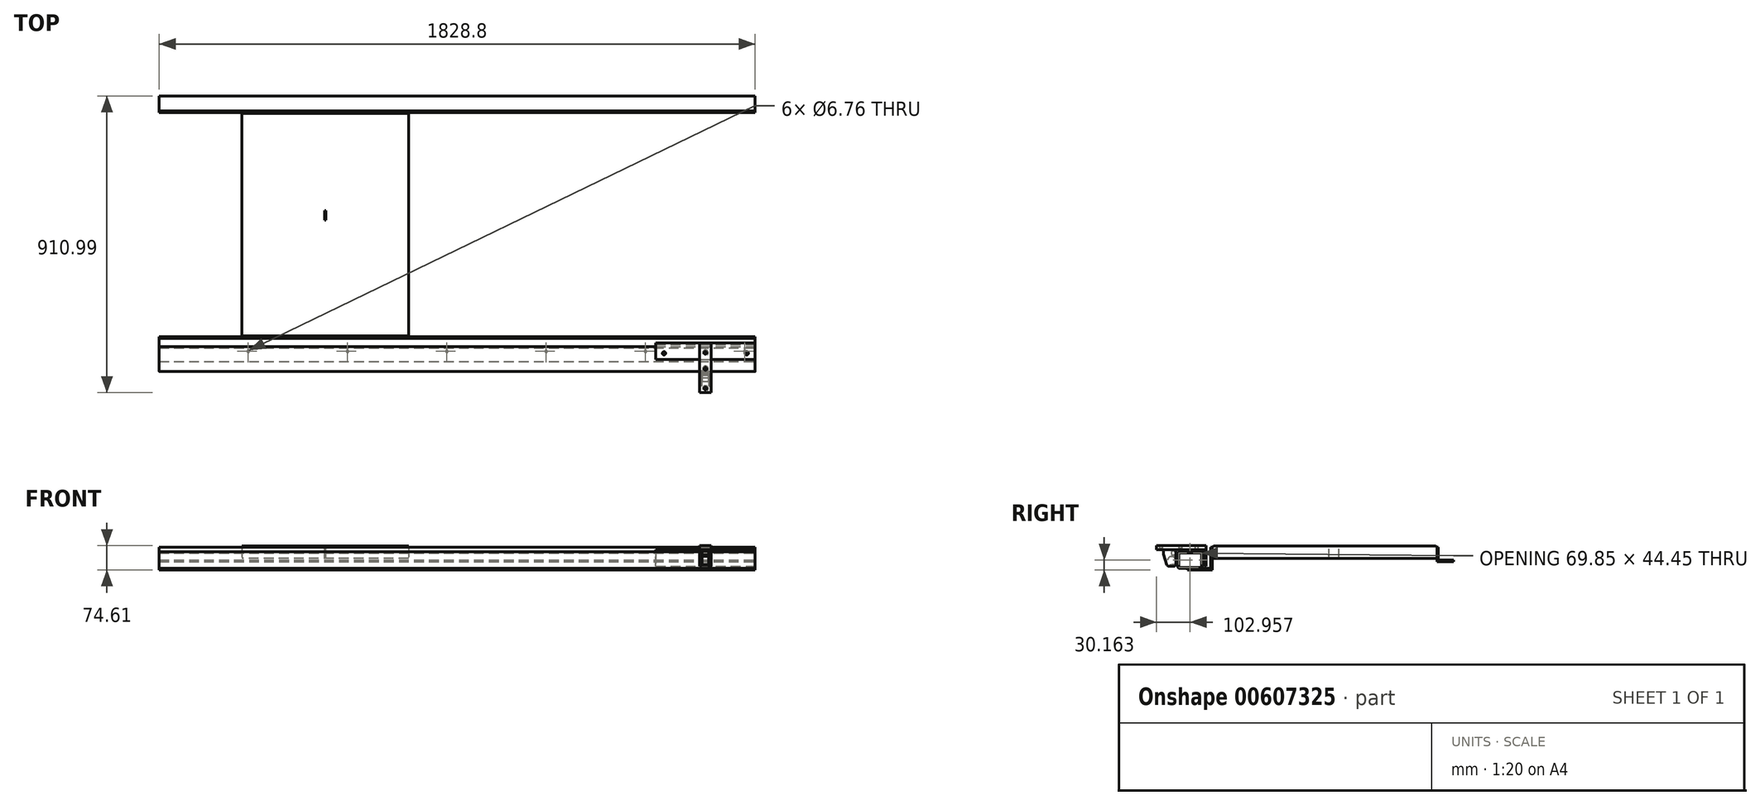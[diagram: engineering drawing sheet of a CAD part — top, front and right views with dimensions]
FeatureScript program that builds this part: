
annotation { "Feature Type Name" : "Feature", "Feature Type Description" : "" }
export const myFeature = defineFeature(function(context is Context, id is Id, definition is map)
    precondition{}
    {
        {
            var Q0;
            Q0=qCreatedBy(makeId("Right.planeOp"),FACE);
            var sketch = newSketch(context, id + "F0", { "sketchPlane" : qUnion([Q0])});
            skLineSegment(sketch, "E0", {"start": v(-76.2, 0) * mm, "end": v(0, 0) * mm});
            skLineSegment(sketch, "E1", {"start": v(0, 0) * mm, "end": v(0, 69.85) * mm});
            skLineSegment(sketch, "E2", {"start": v(0, 69.85) * mm, "end": v(-4.76, 69.85) * mm});
            skLineSegment(sketch, "E3", {"start": v(-4.76, 69.85) * mm, "end": v(-4.76, 4.76) * mm});
            skLineSegment(sketch, "E4", {"start": v(-4.76, 4.76) * mm, "end": v(-76.2, 4.76) * mm});
            skLineSegment(sketch, "E5", {"start": v(-76.2, 4.76) * mm, "end": v(-76.2, 0) * mm});
            skSolve(sketch);
        }
        {
            var Q0;
            Q0 = qSketchRegion(id + "F0", true);
            extrude(context, id + "F1", {"entities" : qUnion([Q0]), "oppositeDirection" : true, "depth" : 1828.8 * mm, "offsetDistance" : 25.4 * mm});
        }
        {
            var Q0;
            Q0=qCreatedBy(makeId("Right.planeOp"),FACE);
            var sketch = newSketch(context, id + "F2", { "sketchPlane" : qUnion([Q0])});
            skLineSegment(sketch, "E6.0", {"start": v(-4.76, 4.76) * mm, "end": v(-76.2, 4.76) * mm});
            skLineSegment(sketch, "E7.bottom", {"start": v(-36.51, 4.76) * mm, "end": v(-100.01, 4.76) * mm});
            skLineSegment(sketch, "E7.top", {"start": v(-36.51, 55.56) * mm, "end": v(-100.01, 55.56) * mm});
            skLineSegment(sketch, "E7.left", {"start": v(-30.16, 11.11) * mm, "end": v(-30.16, 49.21) * mm});
            skLineSegment(sketch, "E7.right", {"start": v(-106.36, 11.11) * mm, "end": v(-106.36, 49.21) * mm});
            skLineSegment(sketch, "E8.bottom", {"start": v(-100.01, 52.39) * mm, "end": v(-36.51, 52.39) * mm});
            skLineSegment(sketch, "E8.top", {"start": v(-100.01, 7.94) * mm, "end": v(-36.51, 7.94) * mm});
            skLineSegment(sketch, "E8.left", {"start": v(-103.19, 49.21) * mm, "end": v(-103.19, 11.11) * mm});
            skLineSegment(sketch, "E8.right", {"start": v(-33.34, 49.21) * mm, "end": v(-33.34, 11.11) * mm});
            skPoint(sketch, "E9.visualSharp", {"position": v(-106.36, 55.56) * mm});
            skArc(sketch, "E9.filletArc", {"start": v(-100.01, 55.56) * mm, "mid": v(-104.5, 53.7) * mm, "end": v(-106.36, 49.21) * mm});
            skPoint(sketch, "E10.visualSharp", {"position": v(-106.36, 4.76) * mm});
            skArc(sketch, "E10.filletArc", {"start": v(-106.36, 11.11) * mm, "mid": v(-104.5, 6.62) * mm, "end": v(-100.01, 4.76) * mm});
            skPoint(sketch, "E11.visualSharp", {"position": v(-30.16, 4.76) * mm});
            skArc(sketch, "E11.filletArc", {"start": v(-36.51, 4.76) * mm, "mid": v(-32.02, 6.62) * mm, "end": v(-30.16, 11.11) * mm});
            skPoint(sketch, "E12.visualSharp", {"position": v(-30.16, 55.56) * mm});
            skArc(sketch, "E12.filletArc", {"start": v(-30.16, 49.21) * mm, "mid": v(-32.02, 53.7) * mm, "end": v(-36.51, 55.56) * mm});
            skPoint(sketch, "E13.visualSharp", {"position": v(-33.34, 52.39) * mm});
            skArc(sketch, "E13.filletArc", {"start": v(-33.34, 49.21) * mm, "mid": v(-34.27, 51.46) * mm, "end": v(-36.51, 52.39) * mm});
            skPoint(sketch, "E14.visualSharp", {"position": v(-103.19, 52.39) * mm});
            skArc(sketch, "E14.filletArc", {"start": v(-100.01, 52.39) * mm, "mid": v(-102.26, 51.46) * mm, "end": v(-103.19, 49.21) * mm});
            skPoint(sketch, "E15.visualSharp", {"position": v(-103.19, 7.94) * mm});
            skArc(sketch, "E15.filletArc", {"start": v(-103.19, 11.11) * mm, "mid": v(-102.26, 8.87) * mm, "end": v(-100.01, 7.94) * mm});
            skPoint(sketch, "E16.visualSharp", {"position": v(-33.34, 7.94) * mm});
            skArc(sketch, "E16.filletArc", {"start": v(-36.51, 7.94) * mm, "mid": v(-34.27, 8.87) * mm, "end": v(-33.34, 11.11) * mm});
            skSolve(sketch);
        }
        {
            var Q0;
            Q0 = qSketchRegion(id + "F2", true);
            extrude(context, id + "F3", {"entities" : qUnion([Q0]), "oppositeDirection" : true, "depth" : 1828.8 * mm, "offsetDistance" : 25.4 * mm});
        }
        {
            var Q0;
            Q0=qCreatedBy(makeId("Right.planeOp"),FACE);
            var sketch = newSketch(context, id + "F4", { "sketchPlane" : qUnion([Q0])});
            skLineSegment(sketch, "E17.0", {"start": v(-36.51, 55.56) * mm, "end": v(-100.01, 55.56) * mm});
            skLineSegment(sketch, "E18.0", {"start": v(-30.16, 11.11) * mm, "end": v(-30.16, 49.21) * mm});
            skLineSegment(sketch, "E19", {"start": v(-69.62, 57.15) * mm, "end": v(-29.93, 57.15) * mm});
            skLineSegment(sketch, "E20", {"start": v(-23.58, 50.8) * mm, "end": v(-23.58, 11.11) * mm});
            skLineSegment(sketch, "E21", {"start": v(-23.58, 11.11) * mm, "end": v(-18.82, 11.11) * mm});
            skLineSegment(sketch, "E22", {"start": v(-18.82, 11.11) * mm, "end": v(-18.82, 61.91) * mm});
            skLineSegment(sketch, "E23", {"start": v(-18.82, 61.91) * mm, "end": v(-69.62, 61.91) * mm});
            skLineSegment(sketch, "E24", {"start": v(-69.62, 61.91) * mm, "end": v(-69.62, 57.15) * mm});
            skPoint(sketch, "E25.visualSharp", {"position": v(-23.58, 57.15) * mm});
            skArc(sketch, "E25.filletArc", {"start": v(-23.58, 50.8) * mm, "mid": v(-25.44, 55.3) * mm, "end": v(-29.93, 57.15) * mm});
            skSolve(sketch);
        }
        {
            var Q0;
            Q0 = qSketchRegion(id + "F4", true);
            extrude(context, id + "F5", {"entities" : qUnion([Q0]), "oppositeDirection" : true, "depth" : 304.8 * mm, "offsetDistance" : 25.4 * mm});
        }
        {
            var Q0;
            Q0=makeQuery(id+"F5.opExtrude","SWEPT_FACE",FACE,{"disambiguationData":[OSD([sQuery(id+"F4.wireOp",EDGE,"E23")])]});
            var sketch = newSketch(context, id + "F6", { "sketchPlane" : qUnion([Q0])});
            skLineSegment(sketch, "E26", {"start": v(-152.4, -18.82) * mm, "end": v(-152.4, -69.62) * mm, "construction": true});
            skLineSegment(sketch, "E27.bottom", {"start": v(-169.86, -18.82) * mm, "end": v(-134.94, -18.82) * mm});
            skLineSegment(sketch, "E27.top", {"start": v(-169.86, -171.22) * mm, "end": v(-134.94, -171.22) * mm});
            skLineSegment(sketch, "E27.left", {"start": v(-169.86, -18.82) * mm, "end": v(-169.86, -171.22) * mm});
            skLineSegment(sketch, "E27.right", {"start": v(-134.94, -18.82) * mm, "end": v(-134.94, -171.22) * mm});
            skSolve(sketch);
        }
        {
            var Q0;
            Q0 = qSketchRegion(id + "F6", true);
            extrude(context, id + "F7", {"entities" : qUnion([Q0]), "operationType" : NewBodyOperationType.ADD, "depth" : 12.7 * mm, "offsetDistance" : 25.4 * mm});
        }
        {
            var Q0;
            Q0=makeQuery(id+"F3.opExtrude","SWEPT_FACE",FACE,{"disambiguationData":[OSD([sQuery(id+"F2.wireOp",EDGE,"E7.right")])]});
            var sketch = newSketch(context, id + "F8", { "sketchPlane" : qUnion([Q0])});
            skLineSegment(sketch, "E28.bottom", {"start": v(-161.93, 47.62) * mm, "end": v(-142.88, 47.62) * mm});
            skLineSegment(sketch, "E28.top", {"start": v(-161.93, 15.87) * mm, "end": v(-142.88, 15.87) * mm});
            skLineSegment(sketch, "E28.left", {"start": v(-161.93, 47.62) * mm, "end": v(-161.93, 15.87) * mm});
            skLineSegment(sketch, "E28.right", {"start": v(-142.88, 47.62) * mm, "end": v(-142.88, 15.87) * mm});
            skPoint(sketch, "E29.0", {"position": v(-152.4, 61.91) * mm});
            skPoint(sketch, "E30", {"position": v(-152.4, 47.62) * mm});
            skLineSegment(sketch, "E31", {"start": v(-152.4, 61.91) * mm, "end": v(-152.4, 47.62) * mm, "construction": true});
            skSolve(sketch);
        }
        {
            var Q0;
            Q0 = qSketchRegion(id + "F8", true);
            extrude(context, id + "F9", {"entities" : qUnion([Q0]), "depth" : 1.59 * mm, "offsetDistance" : 25.4 * mm});
        }
        {
            var Q0;
            Q0=makeQuery(id+"F9.opExtrude","CAP_FACE",FACE,{"disambiguationData":[OSD([sQuery(id+"F8.wireOp",EDGE,"E28.bottom"),sQuery(id+"F8.wireOp",EDGE,"E28.top"),sQuery(id+"F8.wireOp",EDGE,"E28.left"),sQuery(id+"F8.wireOp",EDGE,"E28.right")])],"isStart":false});
            var sketch = newSketch(context, id + "F10", { "sketchPlane" : qUnion([Q0])});
            skLineSegment(sketch, "E32.bottom", {"start": v(-162.75, 48.45) * mm, "end": v(-142.05, 48.45) * mm});
            skLineSegment(sketch, "E32.top", {"start": v(-162.75, 15.05) * mm, "end": v(-142.05, 15.05) * mm});
            skLineSegment(sketch, "E32.left", {"start": v(-162.75, 48.45) * mm, "end": v(-162.75, 15.05) * mm});
            skLineSegment(sketch, "E32.right", {"start": v(-142.05, 48.45) * mm, "end": v(-142.05, 15.05) * mm});
            skSolve(sketch);
        }
        {
            var Q0;
            Q0 = qSketchRegion(id + "F10", true);
            extrude(context, id + "F11", {"entities" : qUnion([Q0]), "depth" : 6.35 * mm, "offsetDistance" : 25.4 * mm});
        }
        {
            var Q0;
            Q0=makeQuery(id+"F11.opExtrude","SWEPT_FACE",FACE,{"disambiguationData":[OSD([sQuery(id+"F10.wireOp",EDGE,"E32.left")])]});
            var sketch = newSketch(context, id + "F12", { "sketchPlane" : qUnion([Q0])});
            skArc(sketch, "E33", {"start": v(119.32, 45.52) * mm, "mid": v(124.16, 56.34) * mm, "end": v(113.3, 51.58) * mm});
            skLineSegment(sketch, "E34.0", {"start": v(110.13, 48.45) * mm, "end": v(107.95, 48.45) * mm});
            skLineSegment(sketch, "E35.0", {"start": v(114.3, 40.76) * mm, "end": v(114.3, 15.05) * mm});
            skLineSegment(sketch, "E36", {"start": v(119.06, 45.52) * mm, "end": v(119.32, 45.52) * mm});
            skLineSegment(sketch, "E37", {"start": v(113.3, 51.58) * mm, "end": v(113.3, 51.63) * mm});
            skPoint(sketch, "E38.orphan", {"position": v(114.3, 48.45) * mm});
            skPoint(sketch, "E39.visualSharp", {"position": v(113.3, 48.45) * mm});
            skArc(sketch, "E39.filletArc", {"start": v(110.13, 48.45) * mm, "mid": v(112.38, 49.38) * mm, "end": v(113.3, 51.63) * mm});
            skPoint(sketch, "E40.visualSharp", {"position": v(114.3, 45.52) * mm});
            skArc(sketch, "E40.filletArc", {"start": v(119.06, 45.52) * mm, "mid": v(115.7, 44.13) * mm, "end": v(114.3, 40.76) * mm});
            skLineSegment(sketch, "E41", {"start": v(110.13, 48.45) * mm, "end": v(114.3, 48.45) * mm});
            skLineSegment(sketch, "E42", {"start": v(114.3, 40.76) * mm, "end": v(114.3, 48.45) * mm});
            skSolve(sketch);
        }
        {
            var Q0;
            Q0 = qSketchRegion(id + "F12", true);
            var Q1;
            Q1=makeQuery(id+"F11.opExtrude","SWEPT_FACE",FACE,{"disambiguationData":[OSD([sQuery(id+"F10.wireOp",EDGE,"E32.right")])]});
            extrude(context, id + "F13", {"entities" : qUnion([Q0]), "operationType" : NewBodyOperationType.ADD, "endBound" : BoundingType.UP_TO_SURFACE, "oppositeDirection" : true, "depth" : 25.4 * mm, "endBoundEntityFace" : qUnion([Q1]), "offsetDistance" : 25.4 * mm});
        }
        {
            var Q0;
            Q0=makeQuery(id+"F5.opExtrude","SWEPT_FACE",FACE,{"disambiguationData":[OSD([sQuery(id+"F4.wireOp",EDGE,"E19")])]});
            var sketch = newSketch(context, id + "F14", { "sketchPlane" : qUnion([Q0])});
            skLineSegment(sketch, "E43", {"start": v(-304.8, 49.78) * mm, "end": v(0, 49.78) * mm, "construction": true});
            skLineSegment(sketch, "E44", {"start": v(-152.4, 32.49) * mm, "end": v(-152.4, 69.62) * mm, "construction": true});
            skPoint(sketch, "E44.startSnap0", {"position": v(-152.4, 49.78) * mm});
            skPoint(sketch, "E45", {"position": v(-152.4, 48.98) * mm});
            skSolve(sketch);
        }
        {
            var Q0;
            Q0=sQuery(id+"F14.wireOp",VERTEX,"E45");
            var Q1;
            Q1=makeQuery(id+"F5.opExtrude","SWEPT_BODY",BODY,{"disambiguationData":[OSD([sQuery(id+"F4.wireOp",EDGE,"E19"),sQuery(id+"F4.wireOp",EDGE,"E20"),sQuery(id+"F4.wireOp",EDGE,"E21"),sQuery(id+"F4.wireOp",EDGE,"E22"),sQuery(id+"F4.wireOp",EDGE,"E23"),sQuery(id+"F4.wireOp",EDGE,"E24"),sQuery(id+"F4.wireOp",EDGE,"E25.filletArc")])]});
            hole(context, id + "F15", {"style" : HoleStyle.C_SINK, "endStyle" : HoleEndStyle.THROUGH, "standardTappedOrClearance" : lookupTablePath({ "standard" : "ANSI", "fit" : "Normal (ASME)", "size" : "5/16", "type" : "Clearance" }), "standardBlindInLast" : lookupTablePath({ "fit" : "Free", "standard" : "ANSI", "size" : "5/16", "type" : "Clearance" }), "holeDiameter" : 8.43 * mm, "cSinkDiameter" : 16.66 * mm, "cSinkAngle" : 82 * degree, "majorDiameter" : 6.35 * mm, "isTappedThrough" : true, "tappedDepth" : 46.05 * mm, "tapClearance" : 3, "locations" : qUnion([Q0]), "scope" : qUnion([Q1])});
        }
        {
            var Q0;
            Q0=makeQuery(id+"F7.opExtrude","CAP_FACE",FACE,{"disambiguationData":[OSD([sQuery(id+"F6.wireOp",EDGE,"E27.bottom"),sQuery(id+"F6.wireOp",EDGE,"E27.top"),sQuery(id+"F6.wireOp",EDGE,"E27.left"),sQuery(id+"F6.wireOp",EDGE,"E27.right")])],"isStart":true});
            var sketch = newSketch(context, id + "F16", { "sketchPlane" : qUnion([Q0])});
            skLineSegment(sketch, "E46", {"start": v(-152.4, 171.22) * mm, "end": v(-152.4, 69.62) * mm, "construction": true});
            skPoint(sketch, "E47", {"position": v(-152.4, 158.52) * mm});
            skPoint(sketch, "E48", {"position": v(-152.4, 98.2) * mm});
            skSolve(sketch);
        }
        {
            var Q0;
            Q0=sQuery(id+"F16.wireOp",VERTEX,"E48");
            var Q1;
            Q1=sQuery(id+"F16.wireOp",VERTEX,"E47");
            var Q2;
            Q2=makeQuery(id+"F5.opExtrude","SWEPT_BODY",BODY,{"disambiguationData":[OSD([sQuery(id+"F4.wireOp",EDGE,"E19"),sQuery(id+"F4.wireOp",EDGE,"E20"),sQuery(id+"F4.wireOp",EDGE,"E21"),sQuery(id+"F4.wireOp",EDGE,"E22"),sQuery(id+"F4.wireOp",EDGE,"E23"),sQuery(id+"F4.wireOp",EDGE,"E24"),sQuery(id+"F4.wireOp",EDGE,"E25.filletArc")])]});
            hole(context, id + "F17", {"style" : HoleStyle.C_SINK, "endStyle" : HoleEndStyle.THROUGH, "standardTappedOrClearance" : lookupTablePath({ "standard" : "ANSI", "fit" : "Normal (ASME)", "size" : "5/16", "type" : "Clearance" }), "standardBlindInLast" : lookupTablePath({ "fit" : "Free", "standard" : "ANSI", "size" : "5/16", "type" : "Clearance" }), "holeDiameter" : 8.43 * mm, "cSinkDiameter" : 16.66 * mm, "cSinkAngle" : 82 * degree, "majorDiameter" : 6.35 * mm, "isTappedThrough" : true, "tappedDepth" : 46.05 * mm, "tapClearance" : 3, "locations" : qUnion([Q0, Q1]), "scope" : qUnion([Q2])});
        }
        {
            var Q0;
            Q0=makeQuery(id+"F1.opExtrude","SWEPT_FACE",FACE,{"disambiguationData":[OSD([sQuery(id+"F0.wireOp",EDGE,"E0")])]});
            var sketch = newSketch(context, id + "F18", { "sketchPlane" : qUnion([Q0])});
            skLineSegment(sketch, "E49", {"start": v(-31.75, 76.2) * mm, "end": v(-31.75, 35.58) * mm, "construction": true});
            skLineSegment(sketch, "E50", {"start": v(0, 44.45) * mm, "end": v(-1828.8, 44.45) * mm, "construction": true});
            skPoint(sketch, "E51", {"position": v(-31.75, 88.9) * mm});
            skPoint(sketch, "E52", {"position": v(-31.75, 44.45) * mm});
            skPoint(sketch, "E53.1.0.0", {"position": v(-336.55, 44.45) * mm});
            skPoint(sketch, "E53.1.1.0", {"position": v(-336.55, 88.9) * mm});
            skPoint(sketch, "E53.2.0.0", {"position": v(-641.35, 44.45) * mm});
            skPoint(sketch, "E53.2.1.0", {"position": v(-641.35, 88.9) * mm});
            skPoint(sketch, "E53.3.0.0", {"position": v(-946.15, 44.45) * mm});
            skPoint(sketch, "E53.3.1.0", {"position": v(-946.15, 88.9) * mm});
            skPoint(sketch, "E53.4.0.0", {"position": v(-1250.95, 44.45) * mm});
            skPoint(sketch, "E53.4.1.0", {"position": v(-1250.95, 88.9) * mm});
            skPoint(sketch, "E53.5.0.0", {"position": v(-1555.75, 44.45) * mm});
            skPoint(sketch, "E53.5.1.0", {"position": v(-1555.75, 88.9) * mm});
            skLineSegment(sketch, "E53.direction1", {"start": v(-31.75, 44.45) * mm, "end": v(-336.55, 44.45) * mm, "construction": true});
            skLineSegment(sketch, "E53.direction2", {"start": v(-31.75, 44.45) * mm, "end": v(-31.75, 88.9) * mm, "construction": true});
            skSolve(sketch);
        }
        {
            var Q0;
            Q0=sQuery(id+"F18.wireOp",VERTEX,"E53.5.1.0");
            var Q1;
            Q1=sQuery(id+"F18.wireOp",VERTEX,"E53.5.0.0");
            var Q2;
            Q2=sQuery(id+"F18.wireOp",VERTEX,"E53.4.1.0");
            var Q3;
            Q3=sQuery(id+"F18.wireOp",VERTEX,"E53.4.0.0");
            var Q4;
            Q4=sQuery(id+"F18.wireOp",VERTEX,"E53.3.1.0");
            var Q5;
            Q5=sQuery(id+"F18.wireOp",VERTEX,"E53.3.0.0");
            var Q6;
            Q6=sQuery(id+"F18.wireOp",VERTEX,"E53.2.1.0");
            var Q7;
            Q7=sQuery(id+"F18.wireOp",VERTEX,"E53.2.0.0");
            var Q8;
            Q8=sQuery(id+"F18.wireOp",VERTEX,"E53.1.1.0");
            var Q9;
            Q9=sQuery(id+"F18.wireOp",VERTEX,"E53.1.0.0");
            var Q10;
            Q10=sQuery(id+"F18.wireOp",VERTEX,"E51");
            var Q11;
            Q11=sQuery(id+"F18.wireOp",VERTEX,"E52");
            var Q12;
            Q12=makeQuery(id+"F1.opExtrude","SWEPT_BODY",BODY,{"disambiguationData":[OSD([sQuery(id+"F0.wireOp",EDGE,"E0"),sQuery(id+"F0.wireOp",EDGE,"E1"),sQuery(id+"F0.wireOp",EDGE,"E2"),sQuery(id+"F0.wireOp",EDGE,"E3"),sQuery(id+"F0.wireOp",EDGE,"E4"),sQuery(id+"F0.wireOp",EDGE,"E5")])]});
            var Q13;
            Q13=makeQuery(id+"F3.opExtrude","SWEPT_BODY",BODY,{"disambiguationData":[OSD([sQuery(id+"F2.wireOp",EDGE,"E7.bottom"),sQuery(id+"F2.wireOp",EDGE,"E7.top"),sQuery(id+"F2.wireOp",EDGE,"E7.left"),sQuery(id+"F2.wireOp",EDGE,"E7.right"),sQuery(id+"F2.wireOp",EDGE,"E8.bottom"),sQuery(id+"F2.wireOp",EDGE,"E8.top"),sQuery(id+"F2.wireOp",EDGE,"E8.left"),sQuery(id+"F2.wireOp",EDGE,"E8.right"),sQuery(id+"F2.wireOp",EDGE,"E9.filletArc"),sQuery(id+"F2.wireOp",EDGE,"E10.filletArc"),sQuery(id+"F2.wireOp",EDGE,"E11.filletArc"),sQuery(id+"F2.wireOp",EDGE,"E12.filletArc"),sQuery(id+"F2.wireOp",EDGE,"E13.filletArc"),sQuery(id+"F2.wireOp",EDGE,"E14.filletArc"),sQuery(id+"F2.wireOp",EDGE,"E15.filletArc"),sQuery(id+"F2.wireOp",EDGE,"E16.filletArc")])]});
            hole(context, id + "F19", {"style" : HoleStyle.SIMPLE, "endStyle" : HoleEndStyle.BLIND_IN_LAST, "standardTappedOrClearance" : lookupTablePath({ "fit" : "Normal", "standard" : "ANSI", "engagement" : "75%", "pitch" : "20 tpi", "size" : "1/4", "type" : "Clearance & tapped" }), "standardBlindInLast" : lookupTablePath({ "standard" : "ANSI", "fit" : "Free", "engagement" : "75%", "pitch" : "20 tpi", "size" : "1/4", "type" : "Clearance & tapped" }), "holeDiameter" : 6.76 * mm, "tapDrillDiameter" : 5.1 * mm, "majorDiameter" : 6.35 * mm, "showTappedDepth" : true, "holeDepth" : 9.52 * mm, "isTappedThrough" : true, "tappedDepth" : 5.7 * mm, "tapClearance" : 3, "locations" : qUnion([Q0, Q1, Q2, Q3, Q4, Q5, Q6, Q7, Q8, Q9, Q10, Q11]), "scope" : qUnion([Q12, Q13])});
        }
        {
            var Q0;
            {var subQ3=sQuery(id+"F4.wireOp",EDGE,"E23");var subQ4=sQuery(id+"F6.wireOp",EDGE,"E27.left");Q0=makeQuery(id+"F7.boolean.opBoolean","SPLIT",FACE,{"disambiguationData":[TD([makeQuery(id+"F7.opExtrude","SWEPT_FACE",FACE,{"disambiguationData":[OSD([subQ4])]})])],"derivedFrom":makeQuery(id+"F5.opExtrude","SWEPT_FACE",FACE,{"disambiguationData":[OSD([subQ3])]})});}
            var sketch = newSketch(context, id + "F20", { "sketchPlane" : qUnion([Q0])});
            skLineSegment(sketch, "E54", {"start": v(-304.8, -50.57) * mm, "end": v(-279.4, -50.57) * mm, "construction": true});
            skLineSegment(sketch, "E55", {"start": v(-279.4, -50.57) * mm, "end": v(-279.4, -69.62) * mm, "construction": true});
            skLineSegment(sketch, "E56.0", {"start": v(0, -18.82) * mm, "end": v(0, -69.62) * mm, "construction": true});
            skLineSegment(sketch, "E57.0", {"start": v(-134.94, -69.62) * mm, "end": v(0, -69.62) * mm, "construction": true});
            skLineSegment(sketch, "E58", {"start": v(0, -50.57) * mm, "end": v(-25.4, -50.57) * mm, "construction": true});
            skLineSegment(sketch, "E59", {"start": v(-25.4, -50.57) * mm, "end": v(-25.4, -69.62) * mm, "construction": true});
            skSolve(sketch);
        }
        {
            var Q0;
            Q0=sQuery(id+"F20.wireOp",VERTEX,"E55.start");
            var Q1;
            Q1=sQuery(id+"F20.wireOp",VERTEX,"E59.start");
            var Q2;
            Q2=makeQuery(id+"F5.opExtrude","SWEPT_BODY",BODY,{"disambiguationData":[OSD([sQuery(id+"F4.wireOp",EDGE,"E19"),sQuery(id+"F4.wireOp",EDGE,"E20"),sQuery(id+"F4.wireOp",EDGE,"E21"),sQuery(id+"F4.wireOp",EDGE,"E22"),sQuery(id+"F4.wireOp",EDGE,"E23"),sQuery(id+"F4.wireOp",EDGE,"E24"),sQuery(id+"F4.wireOp",EDGE,"E25.filletArc")])]});
            hole(context, id + "F21", {"style" : HoleStyle.C_SINK, "endStyle" : HoleEndStyle.BLIND, "holeDiameter" : 7.94 * mm, "cSinkDiameter" : 10.16 * mm, "cSinkAngle" : 82 * degree, "majorDiameter" : 9.52 * mm, "holeDepth" : 6.35 * mm, "isTappedThrough" : true, "tappedDepth" : 46.02 * mm, "tapClearance" : 3, "locations" : qUnion([Q0, Q1]), "scope" : qUnion([Q2])});
        }
        {
            var Q0;
            Q0=makeQuery(id+"F13.boolean.opBoolean","MERGE",FACE,{"derivedFrom":[makeQuery(id+"F11.opExtrude","SWEPT_FACE",FACE,{"disambiguationData":[OSD([sQuery(id+"F10.wireOp",EDGE,"E32.left")])]}),makeQuery(id+"F13.opExtrude","CAP_FACE",FACE,{"disambiguationData":[OSD([sQuery(id+"F12.wireOp",EDGE,"E33"),sQuery(id+"F12.wireOp",EDGE,"E36"),sQuery(id+"F12.wireOp",EDGE,"E39.filletArc"),sQuery(id+"F12.wireOp",EDGE,"E40.filletArc"),sQuery(id+"F12.wireOp",EDGE,"E41"),sQuery(id+"F12.wireOp",EDGE,"E42")])],"isStart":true})]});
            var sketch = newSketch(context, id + "F22", { "sketchPlane" : qUnion([Q0])});
            skArc(sketch, "E60", {"start": v(124.99, 15.93) * mm, "mid": v(136.4, 34.2) * mm, "end": v(114.97, 36.44) * mm});
            skLineSegment(sketch, "E61.0", {"start": v(114.3, 34.49) * mm, "end": v(114.3, 19.1) * mm});
            skPoint(sketch, "E62.orphan", {"position": v(114.3, 40.76) * mm});
            skPoint(sketch, "E63.orphan", {"position": v(114.3, 15.05) * mm});
            skPoint(sketch, "E64.visualSharp", {"position": v(114.3, 35.5) * mm});
            skArc(sketch, "E64.filletArc", {"start": v(114.97, 36.44) * mm, "mid": v(114.47, 35.52) * mm, "end": v(114.3, 34.49) * mm});
            skPoint(sketch, "E65.visualSharp", {"position": v(114.3, 21.77) * mm});
            skLineSegment(sketch, "E66", {"start": v(117.47, 15.93) * mm, "end": v(124.99, 15.93) * mm});
            skPoint(sketch, "E67.visualSharp", {"position": v(114.3, 15.93) * mm});
            skArc(sketch, "E67.filletArc", {"start": v(114.3, 19.1) * mm, "mid": v(115.23, 16.86) * mm, "end": v(117.47, 15.93) * mm});
            skLineSegment(sketch, "E68", {"start": v(124.99, 28.63) * mm, "end": v(126.58, 28.63) * mm});
            skLineSegment(sketch, "E69", {"start": v(124.99, 28.63) * mm, "end": v(115.97, 37.57) * mm});
            skSolve(sketch);
        }
        {
            var Q0;
            Q0=makeQuery(id+"F22.imprint","IMPRINT",FACE,{"disambiguationData":[TD([[makeQuery(id+"F22.imprint","IMPRINT",EDGE,{"derivedFrom":sQuery(id+"F22.wireOp",EDGE,"E60")}),1.0]])]});
            var Q1;
            {var subQ0=sQuery(id+"F10.wireOp",EDGE,"E32.right");Q1=makeQuery(id+"F13.boolean.opBoolean","MERGE",FACE,{"derivedFrom":[makeQuery(id+"F11.opExtrude","SWEPT_FACE",FACE,{"disambiguationData":[OSD([subQ0])]}),makeQuery(id+"F13.opExtrude","CAP_FACE",FACE,{"disambiguationData":[OSD([subQ0])],"isStart":false})]});}
            extrude(context, id + "F23", {"entities" : qUnion([Q0]), "endBound" : BoundingType.UP_TO_SURFACE, "oppositeDirection" : true, "depth" : 25.4 * mm, "endBoundEntityFace" : qUnion([Q1]), "offsetDistance" : 25.4 * mm});
        }
        {
            var Q0;
            Q0=makeQuery(id+"F7.opExtrude","SWEPT_FACE",FACE,{"disambiguationData":[OSD([sQuery(id+"F6.wireOp",EDGE,"E27.left")])]});
            var sketch = newSketch(context, id + "F24", { "sketchPlane" : qUnion([Q0])});
            skLineSegment(sketch, "E70", {"start": v(112.34, 61.91) * mm, "end": v(112.34, 17.46) * mm});
            skLineSegment(sketch, "E71", {"start": v(118.7, 11.11) * mm, "end": v(133.16, 11.11) * mm});
            skLineSegment(sketch, "E72", {"start": v(139.19, 15.45) * mm, "end": v(150.11, 48.23) * mm});
            skLineSegment(sketch, "E73", {"start": v(150.44, 50.24) * mm, "end": v(150.44, 61.91) * mm});
            skLineSegment(sketch, "E74", {"start": v(150.44, 61.91) * mm, "end": v(112.34, 61.91) * mm});
            skPoint(sketch, "E75.visualSharp", {"position": v(112.34, 11.11) * mm});
            skArc(sketch, "E75.filletArc", {"start": v(112.34, 17.46) * mm, "mid": v(114.2, 12.97) * mm, "end": v(118.7, 11.11) * mm});
            skPoint(sketch, "E76.visualSharp", {"position": v(137.74, 11.11) * mm});
            skArc(sketch, "E76.filletArc", {"start": v(133.16, 11.11) * mm, "mid": v(136.88, 12.31) * mm, "end": v(139.19, 15.45) * mm});
            skPoint(sketch, "E77.visualSharp", {"position": v(150.44, 49.21) * mm});
            skArc(sketch, "E77.filletArc", {"start": v(150.11, 48.23) * mm, "mid": v(150.36, 49.23) * mm, "end": v(150.44, 50.24) * mm});
            skSolve(sketch);
        }
        {
            var Q0;
            Q0 = qSketchRegion(id + "F24", true);
            extrude(context, id + "F25", {"entities" : qUnion([Q0]), "oppositeDirection" : true, "depth" : 6.35 * mm, "offsetDistance" : 25.4 * mm});
        }
        {
            var Q0;
            Q0=makeQuery(id+"F7.opExtrude","SWEPT_FACE",FACE,{"disambiguationData":[OSD([sQuery(id+"F6.wireOp",EDGE,"E27.right")])]});
            var sketch = newSketch(context, id + "F26", { "sketchPlane" : qUnion([Q0])});
            skArc(sketch, "E78.0.0", {"start": v(-150.44, 50.24) * mm, "mid": v(-150.36, 49.23) * mm, "end": v(-150.11, 48.23) * mm});
            skLineSegment(sketch, "E78.0.1", {"start": v(-150.11, 48.23) * mm, "end": v(-139.19, 15.45) * mm});
            skArc(sketch, "E78.0.2", {"start": v(-139.19, 15.45) * mm, "mid": v(-136.88, 12.31) * mm, "end": v(-133.16, 11.11) * mm});
            skLineSegment(sketch, "E78.0.3", {"start": v(-133.16, 11.11) * mm, "end": v(-118.7, 11.11) * mm});
            skArc(sketch, "E78.0.4", {"start": v(-118.7, 11.11) * mm, "mid": v(-114.2, 12.97) * mm, "end": v(-112.34, 17.46) * mm});
            skLineSegment(sketch, "E78.0.5", {"start": v(-112.34, 17.46) * mm, "end": v(-112.34, 61.91) * mm});
            skLineSegment(sketch, "E78.0.6", {"start": v(-112.34, 61.91) * mm, "end": v(-150.44, 61.91) * mm});
            skLineSegment(sketch, "E78.0.7", {"start": v(-150.44, 61.91) * mm, "end": v(-150.44, 50.24) * mm});
            skSolve(sketch);
        }
        {
            var Q0;
            Q0 = qSketchRegion(id + "F26", true);
            extrude(context, id + "F27", {"entities" : qUnion([Q0]), "oppositeDirection" : true, "depth" : 6.35 * mm, "offsetDistance" : 25.4 * mm});
        }
        {
            var Q0;
            Q0=makeQuery(id+"F1.opExtrude","CAP_FACE",FACE,{"disambiguationData":[OSD([sQuery(id+"F0.wireOp",EDGE,"E0"),sQuery(id+"F0.wireOp",EDGE,"E1"),sQuery(id+"F0.wireOp",EDGE,"E2"),sQuery(id+"F0.wireOp",EDGE,"E3"),sQuery(id+"F0.wireOp",EDGE,"E4"),sQuery(id+"F0.wireOp",EDGE,"E5")])],"isStart":false});
            cPlane(context, id + "F28", {"entities" : qUnion([Q0]), "cplaneType" : CPlaneType.OFFSET, "offset" : 254 * mm, "oppositeDirection" : true, "width" : 152.4 * mm, "height" : 152.4 * mm});
        }
        {
            var Q0;
            Q0=qCreatedBy(id+"F28.planeOp",FACE);
            var sketch = newSketch(context, id + "F29", { "sketchPlane" : qUnion([Q0])});
            skPoint(sketch, "E79.0", {"position": v(0, 69.85) * mm});
            skLineSegment(sketch, "E80.0", {"start": v(0, 0) * mm, "end": v(0, 69.85) * mm});
            skLineSegment(sketch, "E81", {"start": v(0, 69.85) * mm, "end": v(-3.17, 73.02) * mm});
            skLineSegment(sketch, "E82", {"start": v(-3.17, 73.02) * mm, "end": v(-685.8, 73.02) * mm});
            skPoint(sketch, "E83.start.orphan", {"position": v(-685.8, 0) * mm});
            skPoint(sketch, "E84.end.orphan", {"position": v(-685.8, 69.85) * mm});
            skLineSegment(sketch, "E85", {"start": v(-688.98, 69.85) * mm, "end": v(-688.98, 34.92) * mm});
            skLineSegment(sketch, "E86", {"start": v(-688.98, 34.92) * mm, "end": v(0, 34.92) * mm});
            skLineSegment(sketch, "E87", {"start": v(-685.8, 73.02) * mm, "end": v(-688.98, 69.85) * mm});
            skPoint(sketch, "E88.orphan", {"position": v(-688.98, 73.02) * mm});
            skSolve(sketch);
        }
        {
            var Q0;
            Q0 = qSketchRegion(id + "F29", true);
            extrude(context, id + "F30", {"entities" : qUnion([Q0]), "oppositeDirection" : true, "depth" : 511.17 * mm, "offsetDistance" : 25.4 * mm});
        }
        {
            var Q0;
            Q0=makeQuery(id+"F1.opExtrude","CAP_FACE",FACE,{"disambiguationData":[OSD([sQuery(id+"F0.wireOp",EDGE,"E0"),sQuery(id+"F0.wireOp",EDGE,"E1"),sQuery(id+"F0.wireOp",EDGE,"E2"),sQuery(id+"F0.wireOp",EDGE,"E3"),sQuery(id+"F0.wireOp",EDGE,"E4"),sQuery(id+"F0.wireOp",EDGE,"E5")])],"isStart":true});
            var sketch = newSketch(context, id + "F31", { "sketchPlane" : qUnion([Q0])});
            skPoint(sketch, "E89.0", {"position": v(688.98, 69.85) * mm});
            skLineSegment(sketch, "E90", {"start": v(688.98, 69.85) * mm, "end": v(688.98, 25.4) * mm});
            skLineSegment(sketch, "E91", {"start": v(688.98, 25.4) * mm, "end": v(739.78, 25.4) * mm});
            skLineSegment(sketch, "E92", {"start": v(739.78, 25.4) * mm, "end": v(739.78, 30.16) * mm});
            skLineSegment(sketch, "E93", {"start": v(739.78, 30.16) * mm, "end": v(693.74, 30.16) * mm});
            skLineSegment(sketch, "E94", {"start": v(693.74, 30.16) * mm, "end": v(693.74, 69.85) * mm});
            skLineSegment(sketch, "E95", {"start": v(693.74, 69.85) * mm, "end": v(688.98, 69.85) * mm});
            skSolve(sketch);
        }
        {
            var Q0;
            Q0 = qSketchRegion(id + "F31", true);
            extrude(context, id + "F32", {"entities" : qUnion([Q0]), "oppositeDirection" : true, "depth" : 1828.8 * mm, "offsetDistance" : 25.4 * mm});
        }
        {
            var Q0;
            Q0=makeQuery(id+"F30.opExtrude","SWEPT_FACE",FACE,{"disambiguationData":[OSD([sQuery(id+"F29.wireOp",EDGE,"E82")])]});
            var sketch = newSketch(context, id + "F33", { "sketchPlane" : qUnion([Q0])});
            skLineSegment(sketch, "E96", {"start": v(-1574.8, 388.1) * mm, "end": v(-1319.21, 388.1) * mm});
            skLineSegment(sketch, "E97", {"start": v(-1319.21, 388.1) * mm, "end": v(-1063.62, 388.1) * mm});
            skLineSegment(sketch, "E98", {"start": v(-1319.21, 388.1) * mm, "end": v(-1320.8, 388.1) * mm});
            skLineSegment(sketch, "E99", {"start": v(-1320.8, 388.1) * mm, "end": v(-1320.8, 358.6) * mm});
            skLineSegment(sketch, "E100", {"start": v(-1320.8, 358.6) * mm, "end": v(-1317.62, 358.6) * mm});
            skLineSegment(sketch, "E101", {"start": v(-1317.62, 358.6) * mm, "end": v(-1317.62, 388.1) * mm});
            skSolve(sketch);
        }
        {
            var Q0;
            Q0 = qSketchRegion(id + "F33", true);
            extrude(context, id + "F34", {"entities" : qUnion([Q0]), "operationType" : NewBodyOperationType.REMOVE, "oppositeDirection" : true, "depth" : 50.8 * mm, "offsetDistance" : 25.4 * mm});
        }
    });
